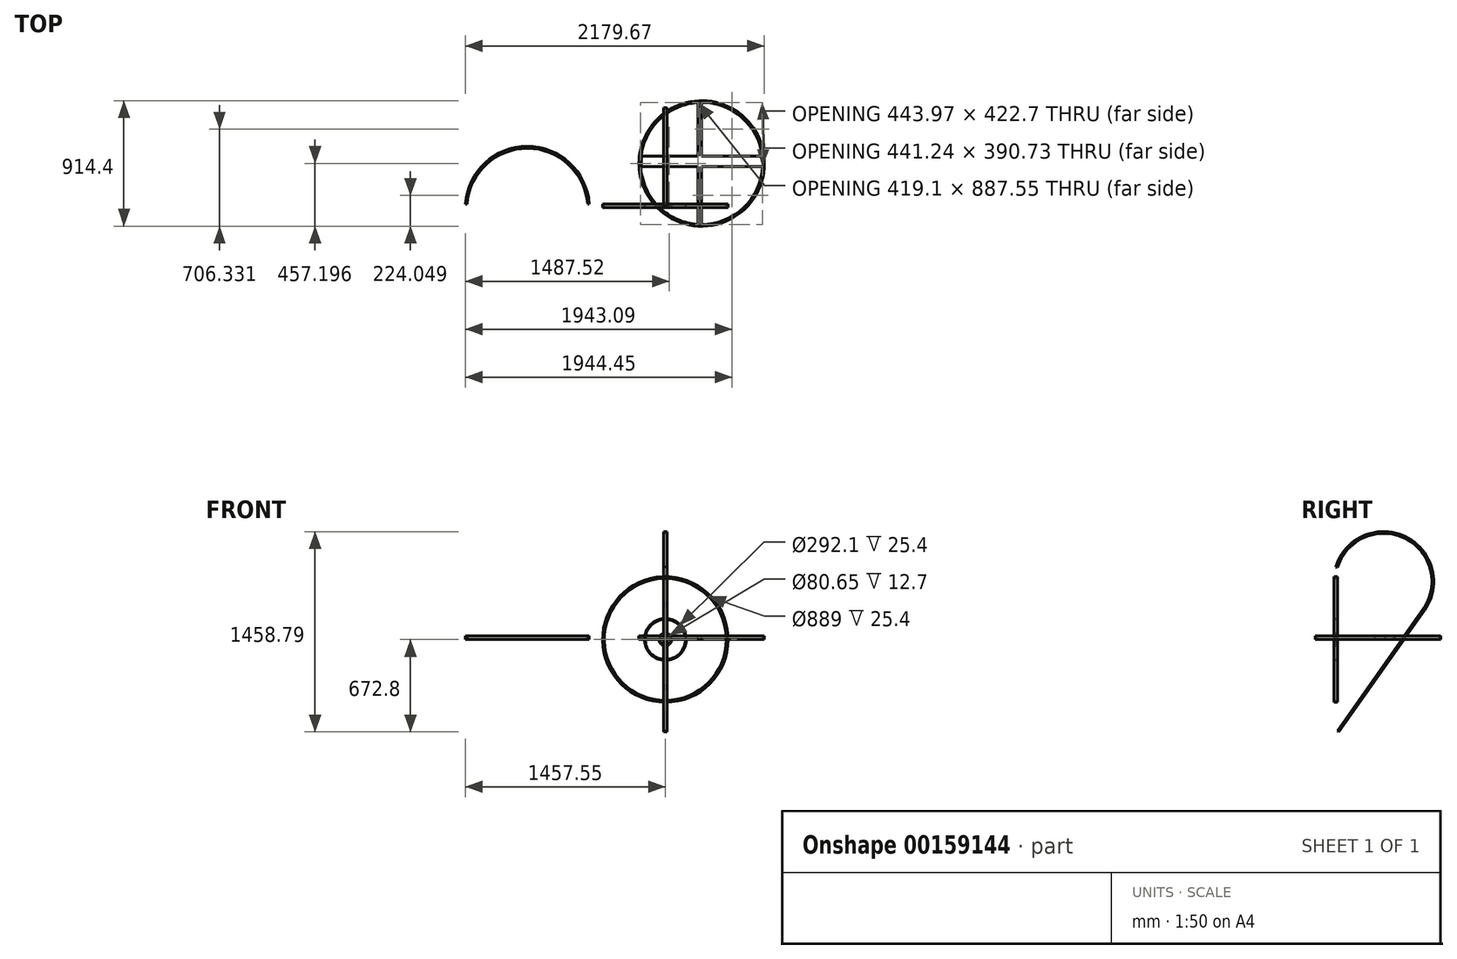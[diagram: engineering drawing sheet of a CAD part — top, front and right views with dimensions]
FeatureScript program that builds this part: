
annotation { "Feature Type Name" : "Feature", "Feature Type Description" : "" }
export const myFeature = defineFeature(function(context is Context, id is Id, definition is map)
    precondition{}
    {
        {
            var Q0;
            Q0=qCreatedBy(makeId("Front.planeOp"),FACE);
            var sketch = newSketch(context, id + "F0", { "sketchPlane" : qUnion([Q0])});
            skCircle(sketch, "E0", {"center": v(0, 0) * mm, "radius": 457.2 * mm});
            skCircle(sketch, "E1.0", {"center": v(0, 0) * mm, "radius": 444.5 * mm});
            skSolve(sketch);
        }
        {
            var Q0;
            Q0 = qSketchRegion(id + "F0", true);
            extrude(context, id + "F1", {"entities" : qUnion([Q0]), "depth" : 25.4 * mm});
        }
        {
            var Q0;
            Q0=qCreatedBy(makeId("Top.planeOp"),FACE);
            var sketch = newSketch(context, id + "F2", { "sketchPlane" : qUnion([Q0])});
            skArc(sketch, "E2", {"start": v(-555.17, 0) * mm, "mid": v(-1006.36, 420.11) * mm, "end": v(-1457.55, 0) * mm});
            skLineSegment(sketch, "E3", {"start": v(-555.17, 0) * mm, "end": v(-566.24, 0) * mm});
            skLineSegment(sketch, "E4", {"start": v(-1457.55, 0) * mm, "end": v(-1446.09, 0) * mm});
            skArc(sketch, "E5", {"start": v(-566.24, 0) * mm, "mid": v(-1006.16, 406.41) * mm, "end": v(-1446.09, 0) * mm});
            skSolve(sketch);
        }
        {
            var Q0;
            Q0=makeQuery(id+"F2.imprint","IMPRINT",FACE,{"disambiguationData":[TD([[makeQuery(id+"F2.imprint","IMPRINT",EDGE,{"derivedFrom":sQuery(id+"F2.wireOp",EDGE,"E2")}),1.0]])]});
            extrude(context, id + "F3", {"entities" : qUnion([Q0]), "depth" : 25.4 * mm});
        }
        {
            var Q0;
            Q0=qCreatedBy(makeId("Front.planeOp"),FACE);
            var sketch = newSketch(context, id + "F4", { "sketchPlane" : qUnion([Q0])});
            skCircle(sketch, "E6", {"center": v(0, 0) * mm, "radius": 146.05 * mm});
            skCircle(sketch, "E7", {"center": v(0, 0) * mm, "radius": 152.4 * mm});
            skSolve(sketch);
        }
        {
            var Q0;
            Q0=makeQuery(id+"F4.imprint","IMPRINT",FACE,{"disambiguationData":[TD([[makeQuery(id+"F4.imprint","IMPRINT",EDGE,{"derivedFrom":sQuery(id+"F4.wireOp",EDGE,"E6")}),-1.0]])]});
            extrude(context, id + "F5", {"entities" : qUnion([Q0]), "depth" : 25.4 * mm});
        }
        {
            var Q0;
            Q0=qCreatedBy(makeId("Front.planeOp"),FACE);
            var sketch = newSketch(context, id + "F6", { "sketchPlane" : qUnion([Q0])});
            skCircle(sketch, "E8", {"center": v(0, 0) * mm, "radius": 40.33 * mm});
            skCircle(sketch, "E9.0", {"center": v(0, 0) * mm, "radius": 46.68 * mm});
            skSolve(sketch);
        }
        {
            var Q0;
            Q0=makeQuery(id+"F6.imprint","IMPRINT",FACE,{"disambiguationData":[TD([[makeQuery(id+"F6.imprint","IMPRINT",EDGE,{"derivedFrom":sQuery(id+"F6.wireOp",EDGE,"E8")}),-1.0]])]});
            var sketch = newSketch(context, id + "F7", { "sketchPlane" : qUnion([Q0])});
            skSolve(sketch);
        }
        {
            var Q0;
            Q0 = qSketchRegion(id + "F7", true);
            var Q1;
            Q1=makeQuery(id+"F6.imprint","IMPRINT",FACE,{"disambiguationData":[TD([[makeQuery(id+"F6.imprint","IMPRINT",EDGE,{"derivedFrom":sQuery(id+"F6.wireOp",EDGE,"E8")}),-1.0]])]});
            extrude(context, id + "F8", {"entities" : qUnion([Q0, Q1]), "depth" : 12.7 * mm});
        }
        {
            var Q0;
            Q0=qCreatedBy(makeId("Right.planeOp"),FACE);
            var sketch = newSketch(context, id + "F9", { "sketchPlane" : qUnion([Q0])});
            skLineSegment(sketch, "E10", {"start": v(0, -665.48) * mm, "end": v(623.75, 219.05) * mm});
            skArc(sketch, "E11", {"start": v(623.75, 219.05) * mm, "mid": v(490.81, 737.57) * mm, "end": v(0, 523.95) * mm});
            skArc(sketch, "E12.0", {"start": v(634.13, 211.73) * mm, "mid": v(496.4, 748.98) * mm, "end": v(-12.15, 527.64) * mm});
            skLineSegment(sketch, "E12.1", {"start": v(10.38, -672.8) * mm, "end": v(634.13, 211.73) * mm});
            skLineSegment(sketch, "E13", {"start": v(-12.15, 527.64) * mm, "end": v(0, 523.95) * mm});
            skLineSegment(sketch, "E14", {"start": v(0, -665.48) * mm, "end": v(10.38, -672.8) * mm});
            skSolve(sketch);
        }
        {
            var Q0;
            Q0 = qSketchRegion(id + "F9", true);
            extrude(context, id + "F10", {"entities" : qUnion([Q0]), "depth" : 25.4 * mm, "symmetric" : true});
        }
        {
            var Q0;
            Q0=qCreatedBy(makeId("Top.planeOp"),FACE);
            var sketch = newSketch(context, id + "F11", { "sketchPlane" : qUnion([Q0])});
            skCircle(sketch, "E15", {"center": v(264.92, 295.62) * mm, "radius": 457.2 * mm});
            skCircle(sketch, "E16.0", {"center": v(264.92, 295.62) * mm, "radius": 444.5 * mm});
            skLineSegment(sketch, "E17", {"start": v(264.92, 740.12) * mm, "end": v(264.92, -148.88) * mm});
            skLineSegment(sketch, "E18.0", {"start": v(239.52, 740.12) * mm, "end": v(239.52, -148.88) * mm});
            skLineSegment(sketch, "E19", {"start": v(264.92, 295.62) * mm, "end": v(617.45, 24.87) * mm});
            skLineSegment(sketch, "E20", {"start": v(264.92, 295.62) * mm, "end": v(586.91, 602.05) * mm});
            skLineSegment(sketch, "E21.0", {"start": v(303.93, 297.68) * mm, "end": v(604.42, 583.65) * mm});
            skLineSegment(sketch, "E21.1", {"start": v(303.93, 297.68) * mm, "end": v(632.92, 45.02) * mm});
            skSolve(sketch);
        }
        {
            var Q0;
            {var subQ0=sQuery(id+"F11.wireOp",EDGE,"E17");var subQ1=sQuery(id+"F11.wireOp",EDGE,"E16.0");var subQ2=makeQuery(id+"F11.imprint","INTERSECT",VERTEX,{"disambiguationData":[OD(0.0)],"derivedFrom":[subQ1,subQ0]});Q0=makeQuery(id+"F11.imprint","IMPRINT",FACE,{"disambiguationData":[TD([[makeQuery(id+"F11.imprint","IMPRINT",EDGE,{"disambiguationData":[TD([[subQ2,-1.0]])],"derivedFrom":subQ1}),1.0]])]});}
            var Q1;
            Q1=makeQuery(id+"F11.imprint","IMPRINT",FACE,{"disambiguationData":[TD([[makeQuery(id+"F11.imprint","IMPRINT",EDGE,{"derivedFrom":sQuery(id+"F11.wireOp",EDGE,"E15")}),1.0]])]});
            extrude(context, id + "F12", {"entities" : qUnion([Q0, Q1]), "depth" : 25.4 * mm});
        }
        {
            var Q0;
            Q0=qCreatedBy(makeId("Top.planeOp"),FACE);
            var sketch = newSketch(context, id + "F13", { "sketchPlane" : qUnion([Q0])});
            skLineSegment(sketch, "E22.bottom", {"start": v(-174, 349.39) * mm, "end": v(715.9, 349.39) * mm});
            skLineSegment(sketch, "E22.top", {"start": v(-174, 273.82) * mm, "end": v(715.9, 273.82) * mm});
            skLineSegment(sketch, "E22.left", {"start": v(-174, 349.39) * mm, "end": v(-174, 273.82) * mm});
            skLineSegment(sketch, "E22.right", {"start": v(715.9, 349.39) * mm, "end": v(715.9, 273.82) * mm});
            skSolve(sketch);
        }
        {
            var Q0;
            Q0=makeQuery(id+"F13.imprint","IMPRINT",FACE,{"disambiguationData":[TD([[makeQuery(id+"F13.imprint","IMPRINT",EDGE,{"derivedFrom":sQuery(id+"F13.wireOp",EDGE,"E22.bottom")}),-1.0]])]});
            extrude(context, id + "F14", {"entities" : qUnion([Q0]), "operationType" : NewBodyOperationType.ADD, "depth" : 25.4 * mm});
        }
    });
